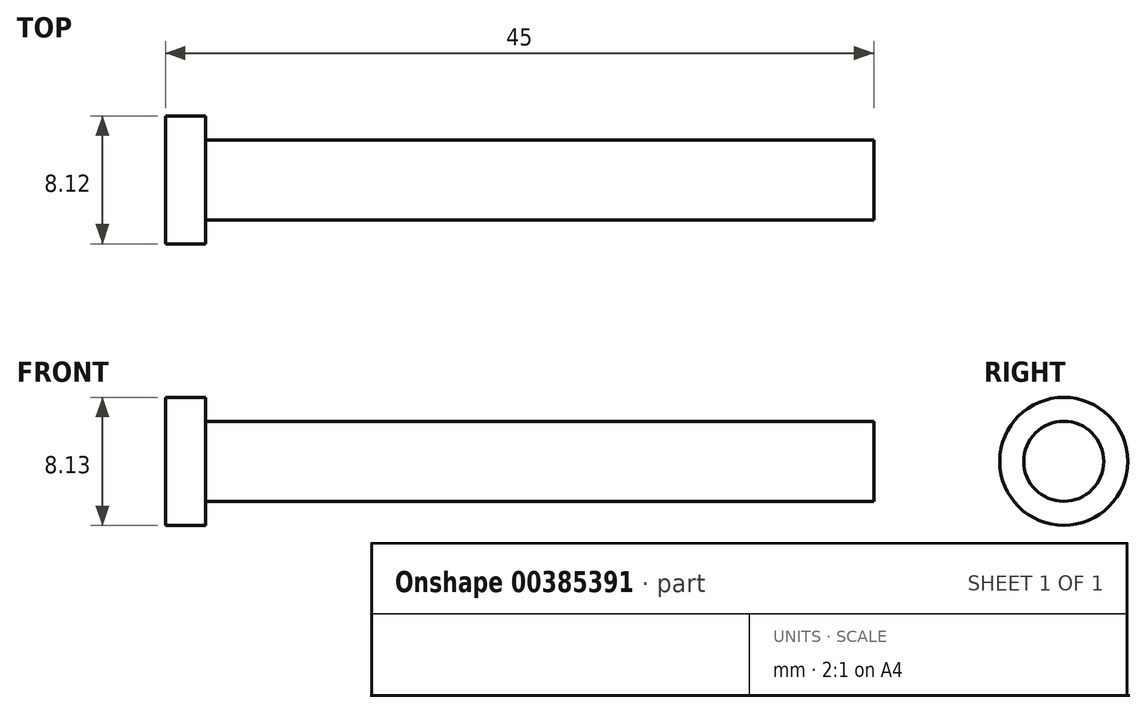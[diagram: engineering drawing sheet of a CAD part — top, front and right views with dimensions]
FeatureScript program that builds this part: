
annotation { "Feature Type Name" : "Feature", "Feature Type Description" : "" }
export const myFeature = defineFeature(function(context is Context, id is Id, definition is map)
    precondition{}
    {
        {
            var Q0;
            Q0=qCreatedBy(makeId("Front.planeOp"),FACE);
            var sketch = newSketch(context, id + "F0", { "sketchPlane" : qUnion([Q0])});
            skLineSegment(sketch, "E0", {"start": v(29.15, 0.34) * mm, "end": v(-13.3, 0.34) * mm});
            skLineSegment(sketch, "E1", {"start": v(-13.3, 0.34) * mm, "end": v(-13.3, 1.86) * mm});
            skLineSegment(sketch, "E2", {"start": v(-13.3, 1.86) * mm, "end": v(-15.85, 1.86) * mm});
            skLineSegment(sketch, "E3", {"start": v(-15.85, 1.86) * mm, "end": v(-15.85, -2.2) * mm});
            skLineSegment(sketch, "E4", {"start": v(-15.85, -2.2) * mm, "end": v(29.15, -2.2) * mm});
            skLineSegment(sketch, "E5", {"start": v(29.15, -2.2) * mm, "end": v(29.15, 0.34) * mm});
            skSolve(sketch);
        }
        {
            var Q0;
            Q0 = qSketchRegion(id + "F0", true);
            var Q1;
            Q1=sQuery(id+"F0.wireOp",EDGE,"E4");
            revolve(context, id + "F1", {"entities" : qUnion([Q0]), "axis" : qUnion([Q1]), "revolveType" : RevolveType.FULL});
        }
    });
